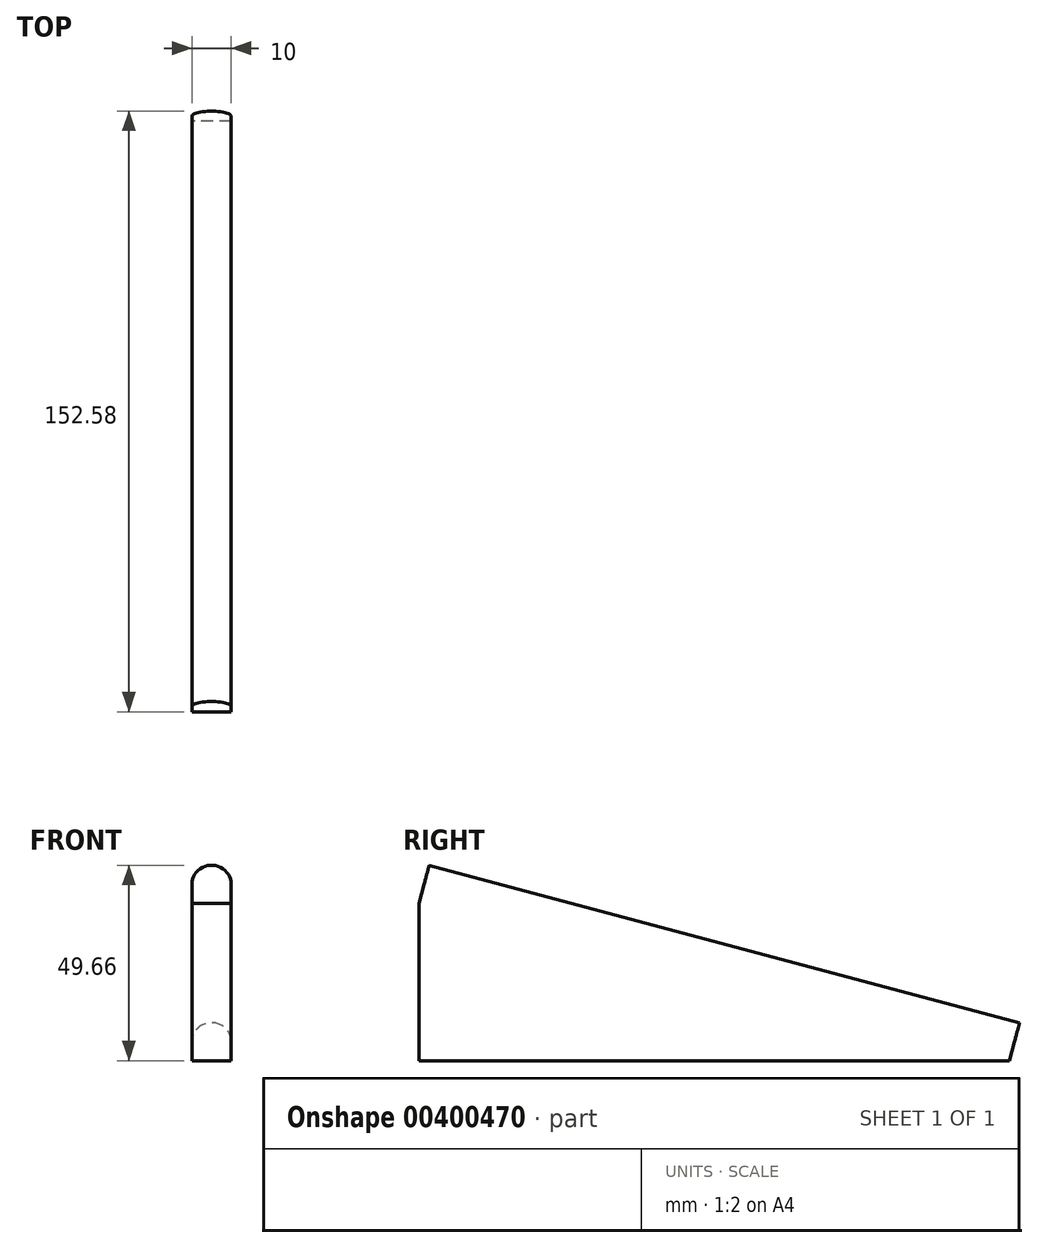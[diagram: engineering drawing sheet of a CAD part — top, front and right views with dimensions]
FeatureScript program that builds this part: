
annotation { "Feature Type Name" : "Feature", "Feature Type Description" : "" }
export const myFeature = defineFeature(function(context is Context, id is Id, definition is map)
    precondition{}
    {
        {
            var Q0;
            Q0=qCreatedBy(makeId("Right.planeOp"),FACE);
            var sketch = newSketch(context, id + "F0", { "sketchPlane" : qUnion([Q0])});
            skLineSegment(sketch, "E0", {"start": v(0, 0) * mm, "end": v(0, 40) * mm});
            skLineSegment(sketch, "E1", {"start": v(0, 40) * mm, "end": v(150, 0) * mm});
            skLineSegment(sketch, "E2", {"start": v(150, 0) * mm, "end": v(0, 0) * mm});
            skLineSegment(sketch, "E3", {"start": v(150, 0) * mm, "end": v(152.58, 9.66) * mm});
            skLineSegment(sketch, "E4", {"start": v(0, 40) * mm, "end": v(2.58, 49.66) * mm});
            skLineSegment(sketch, "E5", {"start": v(2.58, 49.66) * mm, "end": v(152.58, 9.66) * mm});
            skSolve(sketch);
        }
        {
            var Q0;
            Q0 = qSketchRegion(id + "F0", true);
            extrude(context, id + "F1", {"entities" : qUnion([Q0]), "depth" : 10 * mm});
        }
        {
            var Q0;
            Q0=makeQuery(id+"F1.opExtrude","CAP_EDGE",EDGE,{"disambiguationData":[OSD([sQuery(id+"F0.wireOp",EDGE,"E5")])],"isStart":true});
            var Q1;
            Q1=makeQuery(id+"F1.opExtrude","CAP_EDGE",EDGE,{"disambiguationData":[OSD([sQuery(id+"F0.wireOp",EDGE,"E5")])],"isStart":false});
            fillet(context, id + "F2", {"entities" : qUnion([Q0, Q1]), "radius" : 5 * mm, "tangentPropagation" : true, "allowEdgeOverflow" : false});
        }
    });
